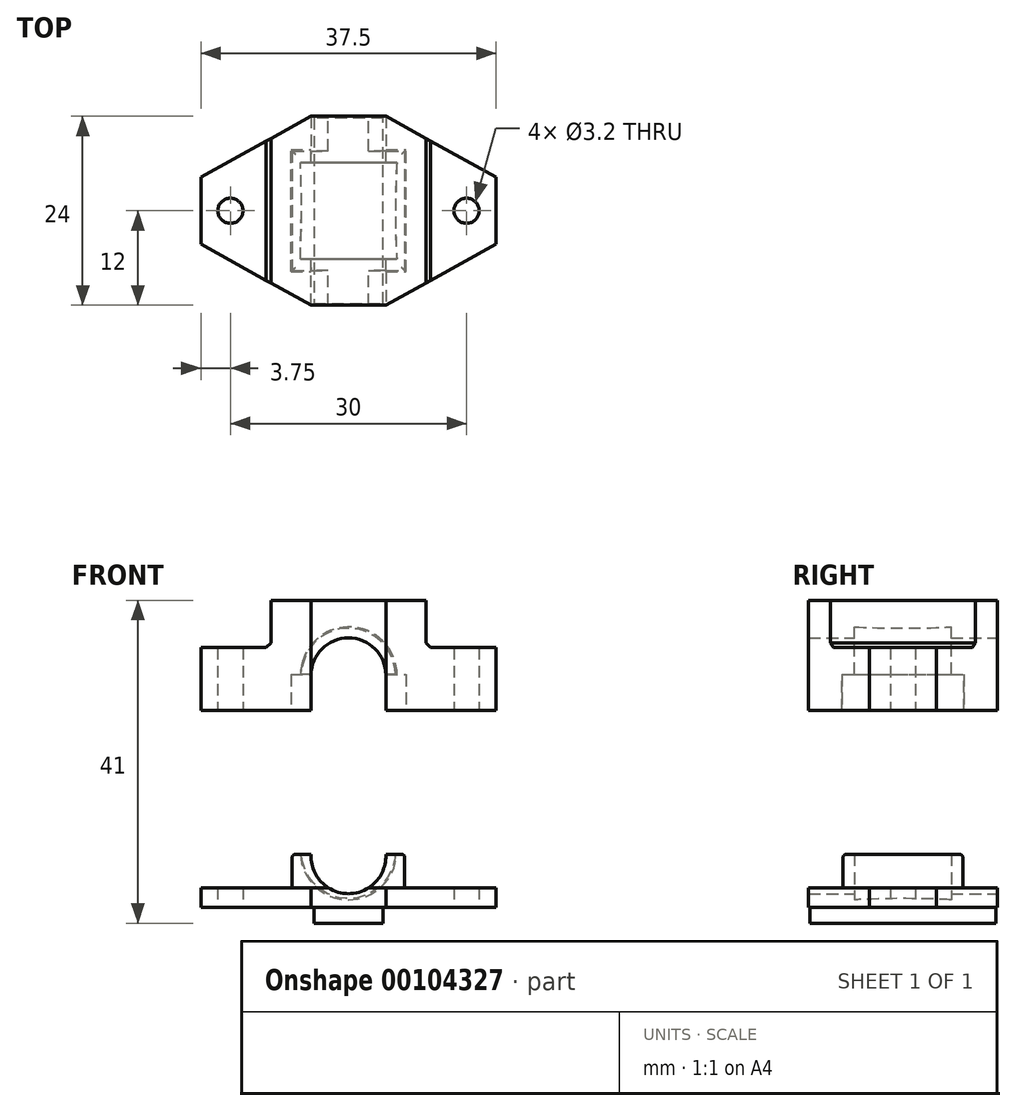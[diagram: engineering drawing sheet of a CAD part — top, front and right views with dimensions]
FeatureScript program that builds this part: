
annotation { "Feature Type Name" : "Feature", "Feature Type Description" : "" }
export const myFeature = defineFeature(function(context is Context, id is Id, definition is map)
    precondition{}
    {
        {
            assignVariable(context, id + "F0", {"name" : "laenge", "anyValue" : 12.3});
        }
        {
            var Q0;
            Q0=qCreatedBy(makeId("Top.planeOp"),FACE);
            var sketch = newSketch(context, id + "F1", { "sketchPlane" : qUnion([Q0])});
            skLineSegment(sketch, "E0", {"start": v(18.75, 4.25) * mm, "end": v(18.75, -4.25) * mm});
            skLineSegment(sketch, "E1", {"start": v(-18.75, 4.25) * mm, "end": v(-18.75, -4.25) * mm});
            skLineSegment(sketch, "E2", {"start": v(-4.75, 12) * mm, "end": v(4.75, 12) * mm});
            skLineSegment(sketch, "E3", {"start": v(-4.75, -12) * mm, "end": v(4.75, -12) * mm});
            skLineSegment(sketch, "E4", {"start": v(4.75, -12) * mm, "end": v(18.75, -4.25) * mm});
            skLineSegment(sketch, "E5", {"start": v(18.75, 4.25) * mm, "end": v(4.75, 12) * mm});
            skLineSegment(sketch, "E6", {"start": v(-4.75, 12) * mm, "end": v(-18.75, 4.25) * mm});
            skLineSegment(sketch, "E7", {"start": v(-18.75, -4.25) * mm, "end": v(-4.75, -12) * mm});
            skCircle(sketch, "E8", {"center": v(-15, 0) * mm, "radius": 1.6 * mm});
            skCircle(sketch, "E9", {"center": v(15, 0) * mm, "radius": 1.6 * mm});
            skSolve(sketch);
        }
        {
            var Q0;
            Q0 = qSketchRegion(id + "F1", true);
            extrude(context, id + "F2", {"entities" : qUnion([Q0]), "depth" : 2.5 * mm});
        }
        {
            var Q0;
            Q0=makeQuery(id+"F2.opExtrude","CAP_FACE",FACE,{"disambiguationData":[OSD([sQuery(id+"F1.wireOp",EDGE,"E0"),sQuery(id+"F1.wireOp",EDGE,"E1"),sQuery(id+"F1.wireOp",EDGE,"E2"),sQuery(id+"F1.wireOp",EDGE,"E3"),sQuery(id+"F1.wireOp",EDGE,"E4"),sQuery(id+"F1.wireOp",EDGE,"E5"),sQuery(id+"F1.wireOp",EDGE,"E6"),sQuery(id+"F1.wireOp",EDGE,"E7"),sQuery(id+"F1.wireOp",EDGE,"E8"),sQuery(id+"F1.wireOp",EDGE,"E9")])],"isStart":true});
            var sketch = newSketch(context, id + "F3", { "sketchPlane" : qUnion([Q0])});
            skLineSegment(sketch, "E10", {"start": v(-4.4, 11.8) * mm, "end": v(4.4, 11.8) * mm});
            skLineSegment(sketch, "E11", {"start": v(4.4, 11.8) * mm, "end": v(4.4, -11.8) * mm});
            skLineSegment(sketch, "E12", {"start": v(4.4, -11.8) * mm, "end": v(-4.38, -11.8) * mm});
            skLineSegment(sketch, "E13", {"start": v(-4.38, -11.8) * mm, "end": v(-4.4, 11.8) * mm});
            skSolve(sketch);
        }
        {
            var Q0;
            Q0 = qSketchRegion(id + "F3", true);
            extrude(context, id + "F4", {"entities" : qUnion([Q0]), "operationType" : NewBodyOperationType.ADD, "depth" : 2 * mm});
        }
        {
            var Q0;
            Q0=qCreatedBy(makeId("Front.planeOp"),FACE);
            var sketch = newSketch(context, id + "F5", { "sketchPlane" : qUnion([Q0])});
            skCircle(sketch, "E14", {"center": v(0, 7.1) * mm, "radius": 5.97 * mm});
            skSolve(sketch);
        }
        {
            var Q0;
            Q0=qCreatedBy(makeId("Front.planeOp"),FACE);
            cPlane(context, id + "F6", {"entities" : qUnion([Q0]), "cplaneType" : CPlaneType.OFFSET, "offset" : ((getVariable(context, 'laenge') / 4) + 0.3) * mm, "width" : 150 * mm, "height" : 150 * mm});
        }
        {
            var Q0;
            Q0=qCreatedBy(id+"F6.planeOp",FACE);
            var sketch = newSketch(context, id + "F7", { "sketchPlane" : qUnion([Q0])});
            skCircle(sketch, "E15", {"center": v(0, 7.1) * mm, "radius": 6.03 * mm});
            skSolve(sketch);
        }
        {
            var Q0;
            Q0=qCreatedBy(makeId("Front.planeOp"),FACE);
            cPlane(context, id + "F8", {"entities" : qUnion([Q0]), "cplaneType" : CPlaneType.OFFSET, "offset" : ((getVariable(context, 'laenge') / 4) + 0.3) * mm, "oppositeDirection" : true, "width" : 150 * mm, "height" : 150 * mm});
        }
        {
            var Q0;
            Q0=qCreatedBy(id+"F8.planeOp",FACE);
            var sketch = newSketch(context, id + "F9", { "sketchPlane" : qUnion([Q0])});
            skCircle(sketch, "E16", {"center": v(0, 7.1) * mm, "radius": 6.03 * mm});
            skSolve(sketch);
        }
        {
            var Q0;
            Q0=qCreatedBy(makeId("Front.planeOp"),FACE);
            cPlane(context, id + "F10", {"entities" : qUnion([Q0]), "cplaneType" : CPlaneType.OFFSET, "offset" : (getVariable(context, 'laenge') / 2) * mm, "width" : 150 * mm, "height" : 150 * mm});
        }
        {
            var Q0;
            Q0=qCreatedBy(id+"F10.planeOp",FACE);
            var sketch = newSketch(context, id + "F11", { "sketchPlane" : qUnion([Q0])});
            skCircle(sketch, "E17", {"center": v(0, 7.1) * mm, "radius": 6.12 * mm});
            skSolve(sketch);
        }
        {
            var Q0;
            Q0=qCreatedBy(makeId("Front.planeOp"),FACE);
            cPlane(context, id + "F12", {"entities" : qUnion([Q0]), "cplaneType" : CPlaneType.OFFSET, "offset" : (getVariable(context, 'laenge') / 2) * mm, "oppositeDirection" : true, "width" : 150 * mm, "height" : 150 * mm});
        }
        {
            var Q0;
            Q0=qCreatedBy(id+"F12.planeOp",FACE);
            var sketch = newSketch(context, id + "F13", { "sketchPlane" : qUnion([Q0])});
            skCircle(sketch, "E18", {"center": v(0, 7.1) * mm, "radius": 6.12 * mm});
            skSolve(sketch);
        }
        {
            var Q0;
            Q0=makeQuery(id+"F2.opExtrude","CAP_FACE",FACE,{"disambiguationData":[OSD([sQuery(id+"F1.wireOp",EDGE,"E0"),sQuery(id+"F1.wireOp",EDGE,"E1"),sQuery(id+"F1.wireOp",EDGE,"E2"),sQuery(id+"F1.wireOp",EDGE,"E3"),sQuery(id+"F1.wireOp",EDGE,"E4"),sQuery(id+"F1.wireOp",EDGE,"E5"),sQuery(id+"F1.wireOp",EDGE,"E6"),sQuery(id+"F1.wireOp",EDGE,"E7"),sQuery(id+"F1.wireOp",EDGE,"E8"),sQuery(id+"F1.wireOp",EDGE,"E9")])],"isStart":false});
            var sketch = newSketch(context, id + "F14", { "sketchPlane" : qUnion([Q0])});
            skLineSegment(sketch, "E19.bottom", {"start": v(-7.15, 7.6) * mm, "end": v(7.15, 7.6) * mm});
            skLineSegment(sketch, "E19.top", {"start": v(-7.15, -7.6) * mm, "end": v(7.15, -7.6) * mm});
            skLineSegment(sketch, "E19.left", {"start": v(-7.15, 7.6) * mm, "end": v(-7.15, -7.6) * mm});
            skLineSegment(sketch, "E19.right", {"start": v(7.15, 7.6) * mm, "end": v(7.15, -7.6) * mm});
            skSolve(sketch);
        }
        {
            var Q0;
            Q0 = qSketchRegion(id + "F14", true);
            extrude(context, id + "F15", {"entities" : qUnion([Q0]), "operationType" : NewBodyOperationType.ADD, "depth" : 4.25 * mm});
        }
        {
            var Q1;
            Q1 = qSketchRegion(id + "F11", true);
            var Q2;
            Q2 = qSketchRegion(id + "F7", true);
            var Q3;
            Q3 = qSketchRegion(id + "F5", true);
            var Q4;
            Q4 = qSketchRegion(id + "F9", true);
            var Q5;
            Q5 = qSketchRegion(id + "F13", true);
            loft(context, id + "F16", {"operationType" : NewBodyOperationType.REMOVE, "sheetProfilesArray" : [{ "sheetProfileEntities" : qUnion([Q1]) }, { "sheetProfileEntities" : qUnion([Q2]) }, { "sheetProfileEntities" : qUnion([Q3]) }, { "sheetProfileEntities" : qUnion([Q4]) }, { "sheetProfileEntities" : qUnion([Q5]) }]});
        }
        {
            var Q0;
            Q0=qCreatedBy(makeId("Top.planeOp"),FACE);
            cPlane(context, id + "F17", {"entities" : qUnion([Q0]), "cplaneType" : CPlaneType.OFFSET, "offset" : 25 * mm, "width" : 150 * mm, "height" : 150 * mm});
        }
        {
            var Q0;
            Q0=qCreatedBy(id+"F17.planeOp",FACE);
            var sketch = newSketch(context, id + "F18", { "sketchPlane" : qUnion([Q0])});
            skLineSegment(sketch, "E20", {"start": v(18.75, 4.25) * mm, "end": v(18.75, -4.25) * mm});
            skLineSegment(sketch, "E21", {"start": v(-18.75, 4.25) * mm, "end": v(-18.75, -4.25) * mm});
            skLineSegment(sketch, "E22", {"start": v(-4.75, 12) * mm, "end": v(4.75, 12) * mm});
            skLineSegment(sketch, "E23", {"start": v(-4.75, -12) * mm, "end": v(4.75, -12) * mm});
            skLineSegment(sketch, "E24", {"start": v(4.75, -12) * mm, "end": v(18.75, -4.25) * mm});
            skLineSegment(sketch, "E25", {"start": v(18.75, 4.25) * mm, "end": v(4.75, 12) * mm});
            skLineSegment(sketch, "E26", {"start": v(-4.75, 12) * mm, "end": v(-18.75, 4.25) * mm});
            skLineSegment(sketch, "E27", {"start": v(-18.75, -4.25) * mm, "end": v(-4.75, -12) * mm});
            skCircle(sketch, "E28", {"center": v(-15, 0) * mm, "radius": 1.6 * mm});
            skCircle(sketch, "E29", {"center": v(15, 0) * mm, "radius": 1.6 * mm});
            skSolve(sketch);
        }
        {
            var Q0;
            Q0 = qSketchRegion(id + "F18", true);
            var Q1;
            Q1=sQuery(id+"F18.wireOp",EDGE,"E20");
            var Q2;
            Q2=sQuery(id+"F18.wireOp",EDGE,"E21");
            var Q3;
            Q3=sQuery(id+"F18.wireOp",EDGE,"E22");
            var Q4;
            Q4=sQuery(id+"F18.wireOp",EDGE,"E23");
            var Q5;
            Q5=sQuery(id+"F18.wireOp",EDGE,"E24");
            var Q6;
            Q6=sQuery(id+"F18.wireOp",EDGE,"E25");
            var Q7;
            Q7=sQuery(id+"F18.wireOp",EDGE,"E26");
            var Q8;
            Q8=sQuery(id+"F18.wireOp",EDGE,"E27");
            var Q9;
            Q9=sQuery(id+"F18.wireOp",EDGE,"E28");
            var Q10;
            Q10=sQuery(id+"F18.wireOp",EDGE,"E29");
            extrude(context, id + "F19", {"entities" : qUnion([Q0]), "surfaceEntities" : qUnion([Q1, Q2, Q3, Q4, Q5, Q6, Q7, Q8, Q9, Q10]), "depth" : 14 * mm});
        }
        {
            var Q0;
            Q0=makeQuery(id+"F19.opExtrude","CAP_FACE",FACE,{"disambiguationData":[OSD([sQuery(id+"F18.wireOp",EDGE,"E20"),sQuery(id+"F18.wireOp",EDGE,"E21"),sQuery(id+"F18.wireOp",EDGE,"E22"),sQuery(id+"F18.wireOp",EDGE,"E23"),sQuery(id+"F18.wireOp",EDGE,"E24"),sQuery(id+"F18.wireOp",EDGE,"E25"),sQuery(id+"F18.wireOp",EDGE,"E26"),sQuery(id+"F18.wireOp",EDGE,"E27"),sQuery(id+"F18.wireOp",EDGE,"E28"),sQuery(id+"F18.wireOp",EDGE,"E29")])],"isStart":true});
            var sketch = newSketch(context, id + "F20", { "sketchPlane" : qUnion([Q0])});
            skLineSegment(sketch, "E30.bottom", {"start": v(-7.3, 7.75) * mm, "end": v(7.3, 7.75) * mm});
            skLineSegment(sketch, "E30.top", {"start": v(-7.3, -7.75) * mm, "end": v(7.3, -7.75) * mm});
            skLineSegment(sketch, "E30.left", {"start": v(-7.3, 7.75) * mm, "end": v(-7.3, -7.75) * mm});
            skLineSegment(sketch, "E30.right", {"start": v(7.3, 7.75) * mm, "end": v(7.3, -7.75) * mm});
            skSolve(sketch);
        }
        {
            var Q0;
            Q0 = qSketchRegion(id + "F20", true);
            extrude(context, id + "F21", {"entities" : qUnion([Q0]), "operationType" : NewBodyOperationType.REMOVE, "oppositeDirection" : true, "depth" : 4.6 * mm});
        }
        {
            var Q0;
            Q0=qCreatedBy(id+"F17.planeOp",FACE);
            cPlane(context, id + "F22", {"entities" : qUnion([Q0]), "cplaneType" : CPlaneType.OFFSET, "offset" : 2 * mm, "oppositeDirection" : true, "width" : 150 * mm, "height" : 150 * mm});
        }
        {
            var Q0;
            Q0=qCreatedBy(makeId("Front.planeOp"),FACE);
            var sketch = newSketch(context, id + "F23", { "sketchPlane" : qUnion([Q0])});
            skCircle(sketch, "E31", {"center": v(0, 29.5) * mm, "radius": 5.97 * mm});
            skSolve(sketch);
        }
        {
            var Q0;
            Q0=qCreatedBy(id+"F6.planeOp",FACE);
            var sketch = newSketch(context, id + "F24", { "sketchPlane" : qUnion([Q0])});
            skCircle(sketch, "E32", {"center": v(-0.04, 29.5) * mm, "radius": 6.03 * mm});
            skSolve(sketch);
        }
        {
            var Q0;
            Q0=qCreatedBy(id+"F8.planeOp",FACE);
            var sketch = newSketch(context, id + "F25", { "sketchPlane" : qUnion([Q0])});
            skCircle(sketch, "E33", {"center": v(0, 29.5) * mm, "radius": 6.03 * mm});
            skSolve(sketch);
        }
        {
            var Q0;
            Q0=qCreatedBy(id+"F10.planeOp",FACE);
            var sketch = newSketch(context, id + "F26", { "sketchPlane" : qUnion([Q0])});
            skCircle(sketch, "E34", {"center": v(0.05, 29.5) * mm, "radius": 6.12 * mm});
            skSolve(sketch);
        }
        {
            var Q0;
            Q0=qCreatedBy(id+"F12.planeOp",FACE);
            var sketch = newSketch(context, id + "F27", { "sketchPlane" : qUnion([Q0])});
            skCircle(sketch, "E35", {"center": v(0.03, 29.5) * mm, "radius": 6.12 * mm});
            skSolve(sketch);
        }
        {
            var Q1;
            Q1 = qSketchRegion(id + "F26", true);
            var Q2;
            Q2 = qSketchRegion(id + "F24", true);
            var Q3;
            Q3 = qSketchRegion(id + "F23", true);
            var Q4;
            Q4 = qSketchRegion(id + "F25", true);
            var Q5;
            Q5 = qSketchRegion(id + "F27", true);
            loft(context, id + "F28", {"operationType" : NewBodyOperationType.REMOVE, "sheetProfilesArray" : [{ "sheetProfileEntities" : qUnion([Q1]) }, { "sheetProfileEntities" : qUnion([Q2]) }, { "sheetProfileEntities" : qUnion([Q3]) }, { "sheetProfileEntities" : qUnion([Q4]) }, { "sheetProfileEntities" : qUnion([Q5]) }]});
        }
        {
            var Q0;
            Q0=qCreatedBy(id+"F6.planeOp",FACE);
            var sketch = newSketch(context, id + "F29", { "sketchPlane" : qUnion([Q0])});
            skCircle(sketch, "E36", {"center": v(0, 29.5) * mm, "radius": 4.75 * mm});
            skCircle(sketch, "E37", {"center": v(0, 6.5) * mm, "radius": 4.75 * mm});
            skSolve(sketch);
        }
        {
            var Q0;
            Q0 = qSketchRegion(id + "F29", true);
            extrude(context, id + "F30", {"entities" : qUnion([Q0]), "operationType" : NewBodyOperationType.REMOVE, "endBound" : BoundingType.THROUGH_ALL, "depth" : 25 * mm, "hasSecondDirection" : true, "secondDirectionBound" : SecondDirectionBoundingType.THROUGH_ALL, "secondDirectionOppositeDirection" : true, "secondDirectionDepth" : 25 * mm});
        }
        {
            var Q0;
            Q0=qCreatedBy(makeId("Front.planeOp"),FACE);
            var sketch = newSketch(context, id + "F31", { "sketchPlane" : qUnion([Q0])});
            skLineSegment(sketch, "E38.bottom", {"start": v(-4.75, 29.5) * mm, "end": v(4.75, 29.5) * mm});
            skLineSegment(sketch, "E38.top", {"start": v(-4.75, 20.66) * mm, "end": v(4.75, 20.66) * mm});
            skLineSegment(sketch, "E38.left", {"start": v(-4.75, 29.5) * mm, "end": v(-4.75, 20.66) * mm});
            skLineSegment(sketch, "E38.right", {"start": v(4.75, 29.5) * mm, "end": v(4.75, 20.66) * mm});
            skSolve(sketch);
        }
        {
            var Q0;
            Q0 = qSketchRegion(id + "F31", true);
            extrude(context, id + "F32", {"entities" : qUnion([Q0]), "operationType" : NewBodyOperationType.REMOVE, "endBound" : BoundingType.THROUGH_ALL, "oppositeDirection" : true, "depth" : 25 * mm, "hasSecondDirection" : true, "secondDirectionBound" : SecondDirectionBoundingType.THROUGH_ALL, "secondDirectionOppositeDirection" : false, "secondDirectionDepth" : 25 * mm});
        }
        {
            var Q0;
            {var subQ0=sQuery(id+"F14.wireOp",EDGE,"E19.left");var subQ1=sQuery(id+"F14.wireOp",EDGE,"E19.top");Q0=makeQuery(id+"F30.boolean.opBoolean","SPLIT",EDGE,{"disambiguationData":[TD([makeQuery(id+"F15.opExtrude","SWEPT_FACE",FACE,{"disambiguationData":[OSD([subQ0])]})])],"derivedFrom":makeQuery(id+"F15.opExtrude","CAP_EDGE",EDGE,{"disambiguationData":[OSD([subQ1])],"isStart":false})});}
            var Q1;
            Q1=makeQuery(id+"F15.opExtrude","CAP_EDGE",EDGE,{"disambiguationData":[OSD([sQuery(id+"F14.wireOp",EDGE,"E19.left")])],"isStart":false});
            var Q2;
            {var subQ0=sQuery(id+"F14.wireOp",EDGE,"E19.right");var subQ1=sQuery(id+"F14.wireOp",EDGE,"E19.top");Q2=makeQuery(id+"F30.boolean.opBoolean","SPLIT",EDGE,{"disambiguationData":[TD([makeQuery(id+"F15.opExtrude","SWEPT_FACE",FACE,{"disambiguationData":[OSD([subQ0])]})])],"derivedFrom":makeQuery(id+"F15.opExtrude","CAP_EDGE",EDGE,{"disambiguationData":[OSD([subQ1])],"isStart":false})});}
            var Q3;
            Q3=makeQuery(id+"F15.opExtrude","CAP_EDGE",EDGE,{"disambiguationData":[OSD([sQuery(id+"F14.wireOp",EDGE,"E19.right")])],"isStart":false});
            var Q4;
            {var subQ0=sQuery(id+"F14.wireOp",EDGE,"E19.bottom");var subQ1=sQuery(id+"F14.wireOp",EDGE,"E19.right");Q4=makeQuery(id+"F30.boolean.opBoolean","SPLIT",EDGE,{"disambiguationData":[TD([makeQuery(id+"F15.opExtrude","SWEPT_FACE",FACE,{"disambiguationData":[OSD([subQ1])]})])],"derivedFrom":makeQuery(id+"F15.opExtrude","CAP_EDGE",EDGE,{"disambiguationData":[OSD([subQ0])],"isStart":false})});}
            var Q5;
            {var subQ0=sQuery(id+"F14.wireOp",EDGE,"E19.bottom");var subQ1=sQuery(id+"F14.wireOp",EDGE,"E19.left");Q5=makeQuery(id+"F30.boolean.opBoolean","SPLIT",EDGE,{"disambiguationData":[TD([makeQuery(id+"F15.opExtrude","SWEPT_FACE",FACE,{"disambiguationData":[OSD([subQ1])]})])],"derivedFrom":makeQuery(id+"F15.opExtrude","CAP_EDGE",EDGE,{"disambiguationData":[OSD([subQ0])],"isStart":false})});}
            fillet(context, id + "F33", {"entities" : qUnion([Q0, Q1, Q2, Q3, Q4, Q5]), "radius" : 0.4 * mm, "tangentPropagation" : true, "allowEdgeOverflow" : false});
        }
        {
            var Q0;
            Q0=makeQuery(id+"F19.opExtrude","CAP_FACE",FACE,{"disambiguationData":[OSD([sQuery(id+"F18.wireOp",EDGE,"E20"),sQuery(id+"F18.wireOp",EDGE,"E21"),sQuery(id+"F18.wireOp",EDGE,"E22"),sQuery(id+"F18.wireOp",EDGE,"E23"),sQuery(id+"F18.wireOp",EDGE,"E24"),sQuery(id+"F18.wireOp",EDGE,"E25"),sQuery(id+"F18.wireOp",EDGE,"E26"),sQuery(id+"F18.wireOp",EDGE,"E27"),sQuery(id+"F18.wireOp",EDGE,"E28"),sQuery(id+"F18.wireOp",EDGE,"E29")])],"isStart":false});
            var sketch = newSketch(context, id + "F34", { "sketchPlane" : qUnion([Q0])});
            skLineSegment(sketch, "E39", {"start": v(-18.75, 4.25) * mm, "end": v(-18.75, -4.25) * mm});
            skLineSegment(sketch, "E40", {"start": v(-18.75, -4.25) * mm, "end": v(-9.85, -9.18) * mm});
            skLineSegment(sketch, "E41", {"start": v(-9.85, -9.18) * mm, "end": v(-9.85, 9.18) * mm});
            skLineSegment(sketch, "E42", {"start": v(-9.85, 9.18) * mm, "end": v(-18.75, 4.25) * mm});
            skLineSegment(sketch, "E43", {"start": v(18.75, -4.25) * mm, "end": v(18.75, 4.25) * mm});
            skLineSegment(sketch, "E44", {"start": v(18.75, 4.25) * mm, "end": v(9.85, 9.18) * mm});
            skLineSegment(sketch, "E45", {"start": v(9.85, 9.18) * mm, "end": v(9.85, -9.18) * mm});
            skLineSegment(sketch, "E46", {"start": v(9.85, -9.18) * mm, "end": v(18.75, -4.25) * mm});
            skSolve(sketch);
        }
        {
            var Q0;
            Q0 = qSketchRegion(id + "F34", true);
            extrude(context, id + "F35", {"entities" : qUnion([Q0]), "operationType" : NewBodyOperationType.REMOVE, "oppositeDirection" : true, "depth" : 6 * mm});
        }
        {
            var Q0;
            Q0=makeQuery(id+"F35.boolean.opBoolean","COPY",EDGE,{"derivedFrom":makeQuery(id+"F35.opExtrude","CAP_EDGE",EDGE,{"disambiguationData":[OSD([sQuery(id+"F34.wireOp",EDGE,"E41")])],"isStart":false})});
            var Q1;
            Q1=makeQuery(id+"F35.boolean.opBoolean","COPY",EDGE,{"derivedFrom":makeQuery(id+"F35.opExtrude","CAP_EDGE",EDGE,{"disambiguationData":[OSD([sQuery(id+"F34.wireOp",EDGE,"E45")])],"isStart":false})});
            chamfer(context, id + "F36", {"entities" : qUnion([Q0, Q1]), "width" : 0.6 * mm, "tangentPropagation" : true});
        }
    });
